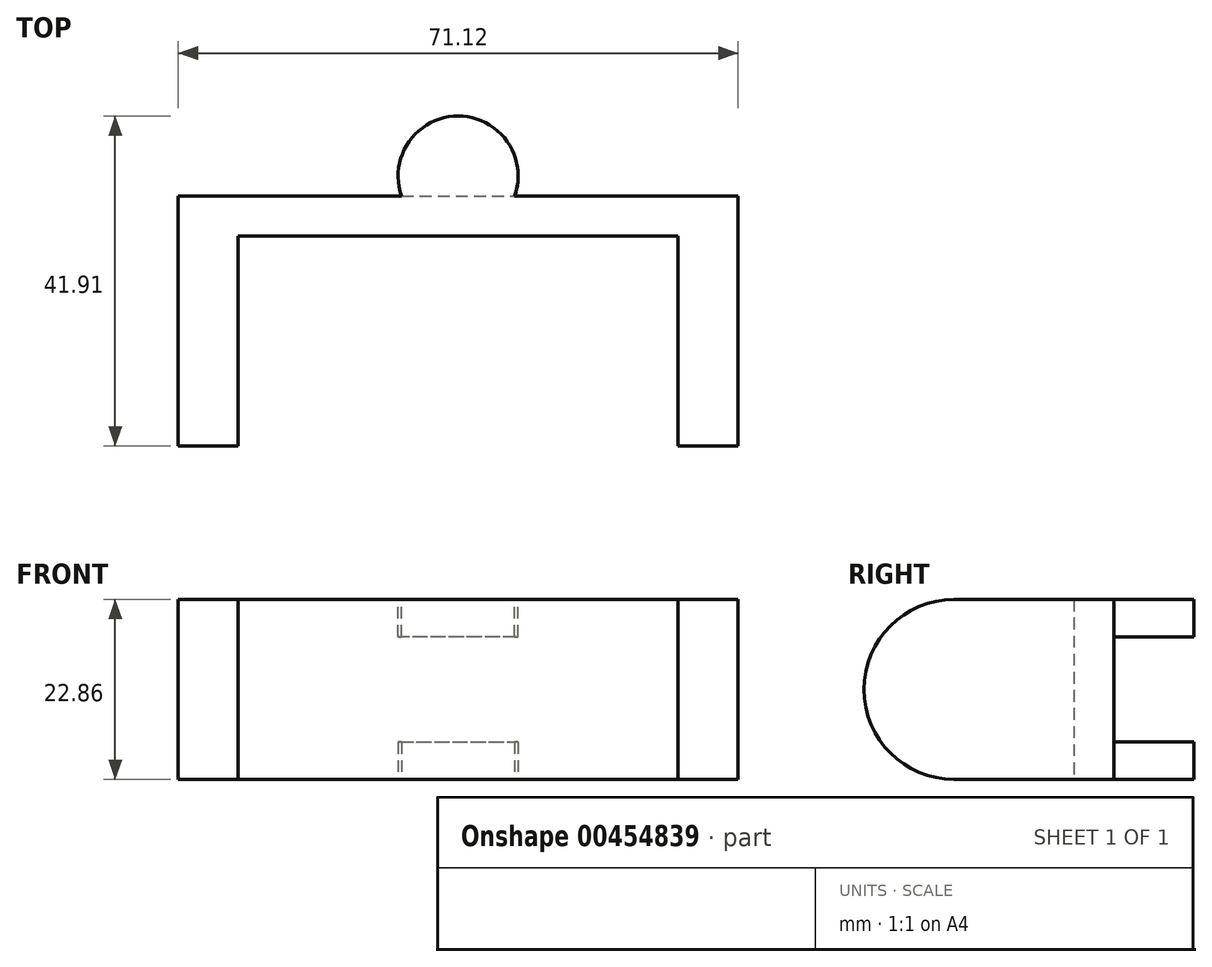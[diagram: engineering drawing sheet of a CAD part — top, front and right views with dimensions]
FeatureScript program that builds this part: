
annotation { "Feature Type Name" : "Feature", "Feature Type Description" : "" }
export const myFeature = defineFeature(function(context is Context, id is Id, definition is map)
    precondition{}
    {
        {
            var Q0;
            Q0=qCreatedBy(makeId("Front.planeOp"),FACE);
            var sketch = newSketch(context, id + "F0", { "sketchPlane" : qUnion([Q0])});
            skLineSegment(sketch, "E0.bottom", {"start": v(-35.56, 11.43) * mm, "end": v(35.56, 11.43) * mm});
            skLineSegment(sketch, "E0.top", {"start": v(-35.56, -11.43) * mm, "end": v(35.56, -11.43) * mm});
            skLineSegment(sketch, "E0.left", {"start": v(-35.56, 11.43) * mm, "end": v(-35.56, -11.43) * mm});
            skLineSegment(sketch, "E0.right", {"start": v(35.56, 11.43) * mm, "end": v(35.56, -11.43) * mm});
            skPoint(sketch, "E0.middle", {"position": v(0, 0) * mm});
            skSolve(sketch);
        }
        {
            var Q0;
            Q0 = qSketchRegion(id + "F0", true);
            extrude(context, id + "F1", {"entities" : qUnion([Q0]), "depth" : 5.08 * mm, "offsetDistance" : 25.4 * mm});
        }
        {
            var Q0;
            Q0=makeQuery(id+"F1.opExtrude","CAP_FACE",FACE,{"disambiguationData":[OSD([sQuery(id+"F0.wireOp",EDGE,"E0.bottom"),sQuery(id+"F0.wireOp",EDGE,"E0.top"),sQuery(id+"F0.wireOp",EDGE,"E0.left"),sQuery(id+"F0.wireOp",EDGE,"E0.right")])],"isStart":false});
            var sketch = newSketch(context, id + "F2", { "sketchPlane" : qUnion([Q0])});
            skLineSegment(sketch, "E1.bottom", {"start": v(-35.56, 11.43) * mm, "end": v(-27.94, 11.43) * mm});
            skLineSegment(sketch, "E1.top", {"start": v(-35.56, -11.43) * mm, "end": v(-27.94, -11.43) * mm});
            skLineSegment(sketch, "E1.left", {"start": v(-35.56, 11.43) * mm, "end": v(-35.56, -11.43) * mm});
            skLineSegment(sketch, "E1.right", {"start": v(-27.94, 11.43) * mm, "end": v(-27.94, -11.43) * mm});
            skLineSegment(sketch, "E2.bottom", {"start": v(35.56, 11.43) * mm, "end": v(27.94, 11.43) * mm});
            skLineSegment(sketch, "E2.top", {"start": v(35.56, -11.43) * mm, "end": v(27.94, -11.43) * mm});
            skLineSegment(sketch, "E2.left", {"start": v(35.56, 11.43) * mm, "end": v(35.56, -11.43) * mm});
            skLineSegment(sketch, "E2.right", {"start": v(27.94, 11.43) * mm, "end": v(27.94, -11.43) * mm});
            skSolve(sketch);
        }
        {
            var Q0;
            Q0=makeQuery(id+"F2.imprint","IMPRINT",FACE,{"disambiguationData":[TD([[makeQuery(id+"F2.imprint","IMPRINT",EDGE,{"derivedFrom":sQuery(id+"F2.wireOp",EDGE,"E1.bottom")}),-1.0]])]});
            var Q1;
            Q1=makeQuery(id+"F2.imprint","IMPRINT",FACE,{"disambiguationData":[TD([[makeQuery(id+"F2.imprint","IMPRINT",EDGE,{"derivedFrom":sQuery(id+"F2.wireOp",EDGE,"E2.bottom")}),-1.0]])]});
            extrude(context, id + "F3", {"entities" : qUnion([Q0, Q1]), "operationType" : NewBodyOperationType.ADD, "depth" : 15.24 * mm, "offsetDistance" : 25.4 * mm});
        }
        {
            var Q0;
            Q0=makeQuery(id+"F3.boolean.opBoolean","MERGE",FACE,{"derivedFrom":[makeQuery(id+"F1.opExtrude","SWEPT_FACE",FACE,{"disambiguationData":[OSD([sQuery(id+"F0.wireOp",EDGE,"E0.right")])]}),makeQuery(id+"F3.opExtrude","SWEPT_FACE",FACE,{"disambiguationData":[OSD([sQuery(id+"F2.wireOp",EDGE,"E2.left")])]})]});
            var sketch = newSketch(context, id + "F4", { "sketchPlane" : qUnion([Q0])});
            skCircle(sketch, "E3", {"center": v(-20.32, 0) * mm, "radius": 11.43 * mm});
            skSolve(sketch);
        }
        {
            var Q0;
            Q0 = qSketchRegion(id + "F4", true);
            extrude(context, id + "F5", {"entities" : qUnion([Q0]), "operationType" : NewBodyOperationType.ADD, "depth" : -7.62 * mm, "offsetDistance" : 25.4 * mm});
        }
        {
            var Q0;
            Q0=makeQuery(id+"F3.boolean.opBoolean","MERGE",FACE,{"derivedFrom":[makeQuery(id+"F1.opExtrude","SWEPT_FACE",FACE,{"disambiguationData":[OSD([sQuery(id+"F0.wireOp",EDGE,"E0.left")])]}),makeQuery(id+"F3.opExtrude","SWEPT_FACE",FACE,{"disambiguationData":[OSD([sQuery(id+"F2.wireOp",EDGE,"E1.left")])]})]});
            var sketch = newSketch(context, id + "F6", { "sketchPlane" : qUnion([Q0])});
            skCircle(sketch, "E4", {"center": v(20.32, 0) * mm, "radius": 11.43 * mm});
            skSolve(sketch);
        }
        {
            var Q0;
            Q0 = qSketchRegion(id + "F6", true);
            extrude(context, id + "F7", {"entities" : qUnion([Q0]), "operationType" : NewBodyOperationType.ADD, "depth" : -7.62 * mm, "offsetDistance" : 25.4 * mm});
        }
        {
            var Q0;
            Q0=makeQuery(id+"F3.boolean.opBoolean","MERGE",FACE,{"derivedFrom":[makeQuery(id+"F1.opExtrude","SWEPT_FACE",FACE,{"disambiguationData":[OSD([sQuery(id+"F0.wireOp",EDGE,"E0.bottom")])]}),makeQuery(id+"F3.opExtrude","SWEPT_FACE",FACE,{"disambiguationData":[OSD([sQuery(id+"F2.wireOp",EDGE,"E1.bottom")])]}),makeQuery(id+"F3.opExtrude","SWEPT_FACE",FACE,{"disambiguationData":[OSD([sQuery(id+"F2.wireOp",EDGE,"E2.bottom")])]})]});
            var sketch = newSketch(context, id + "F8", { "sketchPlane" : qUnion([Q0])});
            skCircle(sketch, "E5", {"center": v(0, 2.54) * mm, "radius": 7.62 * mm});
            skSolve(sketch);
        }
        {
            var Q0;
            Q0 = qSketchRegion(id + "F8", true);
            extrude(context, id + "F9", {"entities" : qUnion([Q0]), "operationType" : NewBodyOperationType.ADD, "depth" : -4.74 * mm, "offsetDistance" : 25.4 * mm});
        }
        {
            var Q0;
            Q0=makeQuery(id+"F3.boolean.opBoolean","MERGE",FACE,{"derivedFrom":[makeQuery(id+"F1.opExtrude","SWEPT_FACE",FACE,{"disambiguationData":[OSD([sQuery(id+"F0.wireOp",EDGE,"E0.top")])]}),makeQuery(id+"F3.opExtrude","SWEPT_FACE",FACE,{"disambiguationData":[OSD([sQuery(id+"F2.wireOp",EDGE,"E1.top")])]}),makeQuery(id+"F3.opExtrude","SWEPT_FACE",FACE,{"disambiguationData":[OSD([sQuery(id+"F2.wireOp",EDGE,"E2.top")])]})]});
            var sketch = newSketch(context, id + "F10", { "sketchPlane" : qUnion([Q0])});
            skCircle(sketch, "E6", {"center": v(0, -2.54) * mm, "radius": 7.62 * mm});
            skSolve(sketch);
        }
        {
            var Q0;
            Q0 = qSketchRegion(id + "F10", true);
            extrude(context, id + "F11", {"entities" : qUnion([Q0]), "operationType" : NewBodyOperationType.ADD, "depth" : -4.74 * mm, "offsetDistance" : 25.4 * mm});
        }
    });
